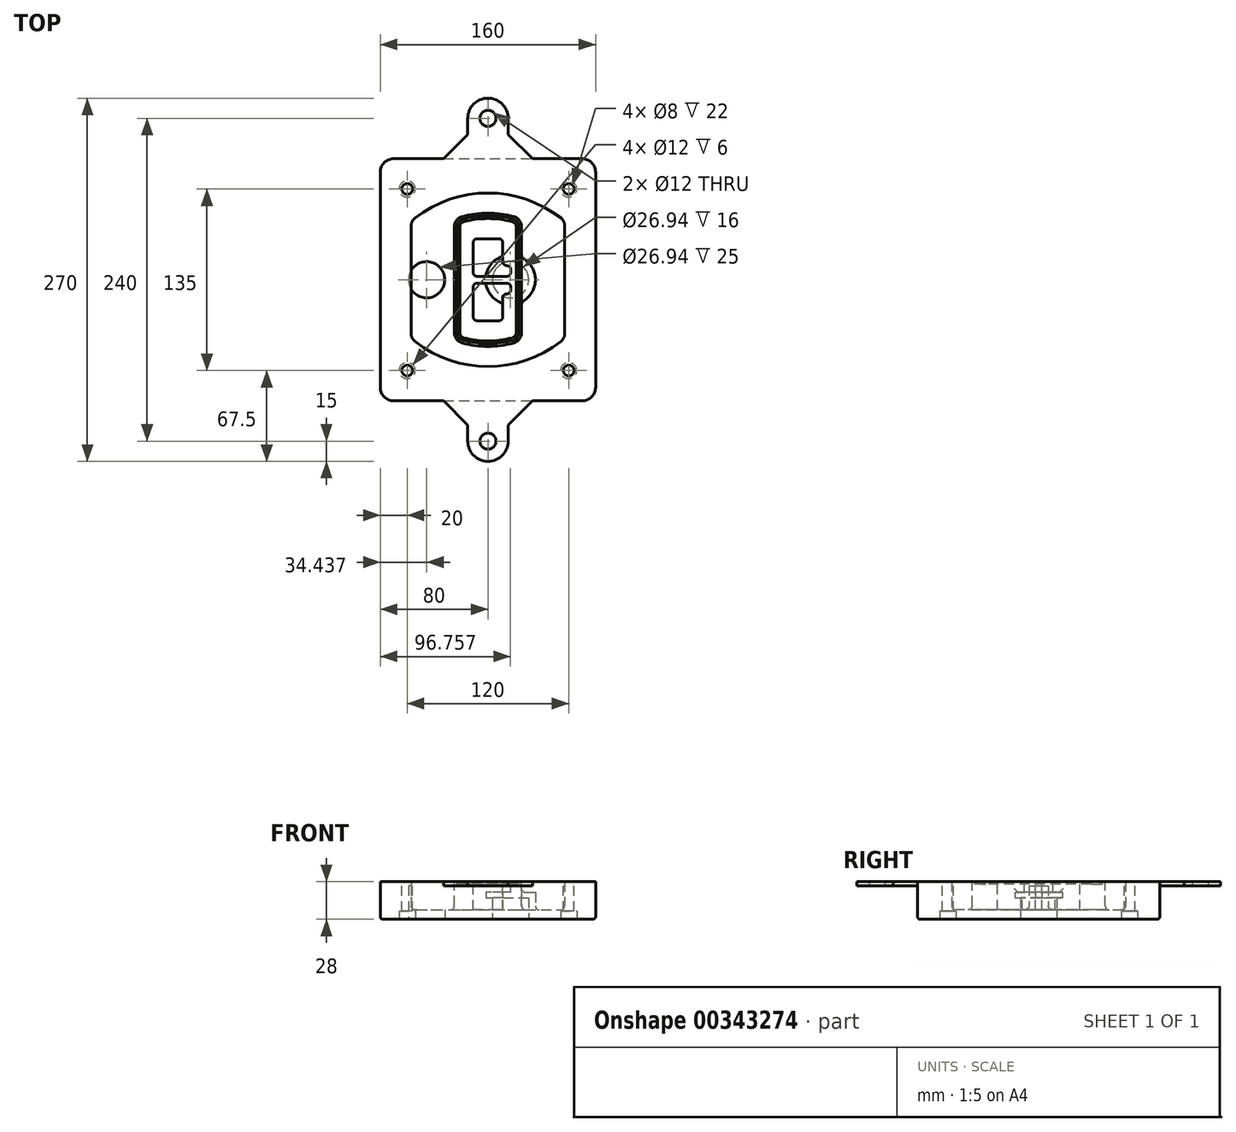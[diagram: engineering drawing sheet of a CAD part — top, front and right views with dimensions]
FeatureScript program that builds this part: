
annotation { "Feature Type Name" : "Feature", "Feature Type Description" : "" }
export const myFeature = defineFeature(function(context is Context, id is Id, definition is map)
    precondition{}
    {
        {
            var Q0;
            Q0=qCreatedBy(makeId("Top.planeOp"),FACE);
            var sketch = newSketch(context, id + "F0", { "sketchPlane" : qUnion([Q0])});
            skPoint(sketch, "E0.rect.middle", {"position": v(0, 0) * mm});
            skLineSegment(sketch, "E1.bottom", {"start": v(-70, -90) * mm, "end": v(70, -90) * mm});
            skLineSegment(sketch, "E1.top", {"start": v(-70, 90) * mm, "end": v(70, 90) * mm});
            skLineSegment(sketch, "E1.left", {"start": v(-80, -80) * mm, "end": v(-80, 80) * mm});
            skLineSegment(sketch, "E1.right", {"start": v(80, -80) * mm, "end": v(80, 80) * mm});
            skLineSegment(sketch, "E2", {"start": v(-80, 90) * mm, "end": v(80, -90) * mm, "construction": true});
            skLineSegment(sketch, "E3", {"start": v(80, 90) * mm, "end": v(-80, -90) * mm, "construction": true});
            skCircle(sketch, "E4", {"center": v(-60, 67.5) * mm, "radius": 4 * mm});
            skCircle(sketch, "E5", {"center": v(60, 67.5) * mm, "radius": 4 * mm});
            skCircle(sketch, "E6", {"center": v(60, -67.5) * mm, "radius": 4 * mm});
            skCircle(sketch, "E7", {"center": v(-60, -67.5) * mm, "radius": 4 * mm});
            skLineSegment(sketch, "E8", {"start": v(-60, 67.5) * mm, "end": v(60, 67.5) * mm, "construction": true});
            skLineSegment(sketch, "E9", {"start": v(60, 67.5) * mm, "end": v(60, -67.5) * mm, "construction": true});
            skLineSegment(sketch, "E10", {"start": v(60, -67.5) * mm, "end": v(-60, -67.5) * mm, "construction": true});
            skLineSegment(sketch, "E11", {"start": v(-60, -67.5) * mm, "end": v(-60, 67.5) * mm, "construction": true});
            skLineSegment(sketch, "E12", {"start": v(-60, 40.3) * mm, "end": v(-60, -40.3) * mm});
            skLineSegment(sketch, "E13", {"start": v(60, 40.3) * mm, "end": v(60, -40.3) * mm});
            skArc(sketch, "E14", {"start": v(56.15, 48.18) * mm, "mid": v(0, 67.5) * mm, "end": v(-56.15, 48.18) * mm});
            skArc(sketch, "E15", {"start": v(-56.15, -48.18) * mm, "mid": v(0, -67.5) * mm, "end": v(56.15, -48.18) * mm});
            skLineSegment(sketch, "E16", {"start": v(-60, 0) * mm, "end": v(60, 0) * mm, "construction": true});
            skPoint(sketch, "E17.visualSharp", {"position": v(-60, -45) * mm});
            skArc(sketch, "E17.filletArc", {"start": v(-60, -40.3) * mm, "mid": v(-58.99, -44.68) * mm, "end": v(-56.15, -48.18) * mm});
            skPoint(sketch, "E18.visualSharp", {"position": v(-60, 45) * mm});
            skArc(sketch, "E18.filletArc", {"start": v(-56.15, 48.18) * mm, "mid": v(-58.99, 44.68) * mm, "end": v(-60, 40.3) * mm});
            skPoint(sketch, "E19.visualSharp", {"position": v(60, 45) * mm});
            skArc(sketch, "E19.filletArc", {"start": v(60, 40.3) * mm, "mid": v(58.99, 44.68) * mm, "end": v(56.15, 48.18) * mm});
            skPoint(sketch, "E20.visualSharp", {"position": v(60, -45) * mm});
            skArc(sketch, "E20.filletArc", {"start": v(56.15, -48.18) * mm, "mid": v(58.99, -44.68) * mm, "end": v(60, -40.3) * mm});
            skPoint(sketch, "E21.visualSharp", {"position": v(-80, 90) * mm});
            skArc(sketch, "E21.filletArc", {"start": v(-70, 90) * mm, "mid": v(-77.07, 87.07) * mm, "end": v(-80, 80) * mm});
            skPoint(sketch, "E22.visualSharp", {"position": v(80, 90) * mm});
            skArc(sketch, "E22.filletArc", {"start": v(80, 80) * mm, "mid": v(77.07, 87.07) * mm, "end": v(70, 90) * mm});
            skPoint(sketch, "E23.visualSharp", {"position": v(80, -90) * mm});
            skArc(sketch, "E23.filletArc", {"start": v(70, -90) * mm, "mid": v(77.07, -87.07) * mm, "end": v(80, -80) * mm});
            skPoint(sketch, "E24.visualSharp", {"position": v(-80, -90) * mm});
            skArc(sketch, "E24.filletArc", {"start": v(-80, -80) * mm, "mid": v(-77.07, -87.07) * mm, "end": v(-70, -90) * mm});
            skArc(sketch, "E25.0", {"start": v(57, 40.3) * mm, "mid": v(56.3, 43.36) * mm, "end": v(54.3, 45.81) * mm});
            skLineSegment(sketch, "E25.1", {"start": v(57, 40.3) * mm, "end": v(57, -40.3) * mm});
            skArc(sketch, "E25.2", {"start": v(54.3, -45.81) * mm, "mid": v(56.3, -43.36) * mm, "end": v(57, -40.3) * mm});
            skArc(sketch, "E25.3", {"start": v(-54.3, -45.81) * mm, "mid": v(0, -64.5) * mm, "end": v(54.3, -45.81) * mm});
            skArc(sketch, "E25.4", {"start": v(-57, -40.3) * mm, "mid": v(-56.3, -43.36) * mm, "end": v(-54.3, -45.81) * mm});
            skArc(sketch, "E25.5", {"start": v(54.3, 45.81) * mm, "mid": v(0, 64.5) * mm, "end": v(-54.3, 45.81) * mm});
            skLineSegment(sketch, "E25.6", {"start": v(-57, 40.3) * mm, "end": v(-57, -40.3) * mm});
            skArc(sketch, "E25.7", {"start": v(-54.3, 45.81) * mm, "mid": v(-56.3, 43.36) * mm, "end": v(-57, 40.3) * mm});
            skArc(sketch, "E26.0", {"start": v(-58.62, 51.33) * mm, "mid": v(-62.58, 46.43) * mm, "end": v(-64, 40.3) * mm});
            skArc(sketch, "E26.1", {"start": v(58.62, 51.33) * mm, "mid": v(0, 71.5) * mm, "end": v(-58.62, 51.33) * mm});
            skArc(sketch, "E26.2", {"start": v(64, 40.3) * mm, "mid": v(62.58, 46.43) * mm, "end": v(58.62, 51.33) * mm});
            skLineSegment(sketch, "E26.3", {"start": v(64, 40.3) * mm, "end": v(64, -40.3) * mm});
            skArc(sketch, "E26.4", {"start": v(58.62, -51.33) * mm, "mid": v(62.58, -46.43) * mm, "end": v(64, -40.3) * mm});
            skLineSegment(sketch, "E26.5", {"start": v(-64, 40.3) * mm, "end": v(-64, -40.3) * mm});
            skArc(sketch, "E26.6", {"start": v(-58.62, -51.33) * mm, "mid": v(0, -71.5) * mm, "end": v(58.62, -51.33) * mm});
            skArc(sketch, "E26.7", {"start": v(-64, -40.3) * mm, "mid": v(-62.58, -46.43) * mm, "end": v(-58.62, -51.33) * mm});
            skSolve(sketch);
        }
        {
            var Q0;
            Q0=makeQuery(id+"F0.imprint","IMPRINT",FACE,{"disambiguationData":[TD([[makeQuery(id+"F0.imprint","IMPRINT",EDGE,{"derivedFrom":sQuery(id+"F0.wireOp",EDGE,"E1.bottom")}),1.0]])]});
            var Q1;
            Q1=makeQuery(id+"F0.imprint","IMPRINT",FACE,{"disambiguationData":[TD([[makeQuery(id+"F0.imprint","IMPRINT",EDGE,{"derivedFrom":sQuery(id+"F0.wireOp",EDGE,"E12")}),1.0]])]});
            var Q2;
            Q2=makeQuery(id+"F0.imprint","IMPRINT",FACE,{"disambiguationData":[TD([[makeQuery(id+"F0.imprint","IMPRINT",EDGE,{"derivedFrom":sQuery(id+"F0.wireOp",EDGE,"E25.0")}),1.0]])]});
            var Q3;
            Q3=makeQuery(id+"F0.imprint","IMPRINT",FACE,{"disambiguationData":[TD([[makeQuery(id+"F0.imprint","IMPRINT",EDGE,{"derivedFrom":sQuery(id+"F0.wireOp",EDGE,"E12")}),-1.0]])]});
            extrude(context, id + "F1", {"entities" : qUnion([Q0, Q1, Q2, Q3]), "oppositeDirection" : true, "depth" : 25 * mm});
        }
        {
            var Q0;
            Q0=makeQuery(id+"F0.imprint","IMPRINT",FACE,{"disambiguationData":[TD([[makeQuery(id+"F0.imprint","IMPRINT",EDGE,{"derivedFrom":sQuery(id+"F0.wireOp",EDGE,"E12")}),1.0]])]});
            extrude(context, id + "F2", {"entities" : qUnion([Q0]), "operationType" : NewBodyOperationType.ADD, "depth" : 3 * mm});
        }
        {
            var Q0;
            Q0=makeQuery(id+"F0.imprint","IMPRINT",FACE,{"disambiguationData":[TD([[makeQuery(id+"F0.imprint","IMPRINT",EDGE,{"derivedFrom":sQuery(id+"F0.wireOp",EDGE,"E25.0")}),1.0]])]});
            extrude(context, id + "F3", {"entities" : qUnion([Q0]), "operationType" : NewBodyOperationType.REMOVE, "oppositeDirection" : true, "depth" : 18 * mm});
        }
        {
            var Q0;
            Q0=makeQuery(id+"F2.opExtrude","CAP_FACE",FACE,{"disambiguationData":[OSD([sQuery(id+"F0.wireOp",EDGE,"E12"),sQuery(id+"F0.wireOp",EDGE,"E13"),sQuery(id+"F0.wireOp",EDGE,"E14"),sQuery(id+"F0.wireOp",EDGE,"E15"),sQuery(id+"F0.wireOp",EDGE,"E17.filletArc"),sQuery(id+"F0.wireOp",EDGE,"E18.filletArc"),sQuery(id+"F0.wireOp",EDGE,"E19.filletArc"),sQuery(id+"F0.wireOp",EDGE,"E20.filletArc"),sQuery(id+"F0.wireOp",EDGE,"E25.0"),sQuery(id+"F0.wireOp",EDGE,"E25.1"),sQuery(id+"F0.wireOp",EDGE,"E25.2"),sQuery(id+"F0.wireOp",EDGE,"E25.3"),sQuery(id+"F0.wireOp",EDGE,"E25.4"),sQuery(id+"F0.wireOp",EDGE,"E25.5"),sQuery(id+"F0.wireOp",EDGE,"E25.6"),sQuery(id+"F0.wireOp",EDGE,"E25.7")])],"isStart":false});
            var sketch = newSketch(context, id + "F4", { "sketchPlane" : qUnion([Q0])});
            skArc(sketch, "E27.0", {"start": v(-19.08, -46.97) * mm, "mid": v(0, -49.5) * mm, "end": v(19.08, -46.97) * mm});
            skArc(sketch, "E28.0", {"start": v(19.08, 46.97) * mm, "mid": v(0, 49.5) * mm, "end": v(-19.08, 46.97) * mm});
            skLineSegment(sketch, "E29", {"start": v(-25, 39.25) * mm, "end": v(-25, -39.25) * mm});
            skLineSegment(sketch, "E30", {"start": v(25, 39.25) * mm, "end": v(25, -39.25) * mm});
            skLineSegment(sketch, "E31", {"start": v(-25, 45.1) * mm, "end": v(25, 45.1) * mm, "construction": true});
            skLineSegment(sketch, "E32", {"start": v(-25, -45.1) * mm, "end": v(25, -45.1) * mm, "construction": true});
            skPoint(sketch, "E33.visualSharp", {"position": v(-25, 45.1) * mm});
            skArc(sketch, "E33.filletArc", {"start": v(-19.08, 46.97) * mm, "mid": v(-23.35, 44.11) * mm, "end": v(-25, 39.25) * mm});
            skPoint(sketch, "E34.visualSharp", {"position": v(25, 45.1) * mm});
            skArc(sketch, "E34.filletArc", {"start": v(25, 39.25) * mm, "mid": v(23.35, 44.11) * mm, "end": v(19.08, 46.97) * mm});
            skPoint(sketch, "E35.visualSharp", {"position": v(25, -45.1) * mm});
            skArc(sketch, "E35.filletArc", {"start": v(19.08, -46.97) * mm, "mid": v(23.35, -44.11) * mm, "end": v(25, -39.25) * mm});
            skPoint(sketch, "E36.visualSharp", {"position": v(-25, -45.1) * mm});
            skArc(sketch, "E36.filletArc", {"start": v(-25, -39.25) * mm, "mid": v(-23.35, -44.11) * mm, "end": v(-19.08, -46.97) * mm});
            skArc(sketch, "E37.0", {"start": v(54.3, 45.81) * mm, "mid": v(0, 64.5) * mm, "end": v(-54.3, 45.81) * mm});
            skArc(sketch, "E37.1", {"start": v(-54.3, 45.81) * mm, "mid": v(-56.3, 43.36) * mm, "end": v(-57, 40.3) * mm});
            skLineSegment(sketch, "E37.2", {"start": v(-57, 40.3) * mm, "end": v(-57, -40.3) * mm});
            skArc(sketch, "E37.3", {"start": v(-57, -40.3) * mm, "mid": v(-56.3, -43.36) * mm, "end": v(-54.3, -45.81) * mm});
            skArc(sketch, "E37.4", {"start": v(-54.3, -45.81) * mm, "mid": v(0, -64.5) * mm, "end": v(54.3, -45.81) * mm});
            skArc(sketch, "E37.5", {"start": v(54.3, -45.81) * mm, "mid": v(56.3, -43.36) * mm, "end": v(57, -40.3) * mm});
            skLineSegment(sketch, "E37.6", {"start": v(57, 40.3) * mm, "end": v(57, -40.3) * mm});
            skArc(sketch, "E37.7", {"start": v(57, 40.3) * mm, "mid": v(56.3, 43.36) * mm, "end": v(54.3, 45.81) * mm});
            skLineSegment(sketch, "E38.0", {"start": v(23, 39.25) * mm, "end": v(23, -39.25) * mm});
            skArc(sketch, "E38.1", {"start": v(18.56, -45.04) * mm, "mid": v(21.76, -42.9) * mm, "end": v(23, -39.25) * mm});
            skArc(sketch, "E38.2", {"start": v(-18.56, -45.04) * mm, "mid": v(0, -47.5) * mm, "end": v(18.56, -45.04) * mm});
            skArc(sketch, "E38.3", {"start": v(-23, -39.25) * mm, "mid": v(-21.76, -42.9) * mm, "end": v(-18.56, -45.04) * mm});
            skLineSegment(sketch, "E38.4", {"start": v(-23, 39.25) * mm, "end": v(-23, -39.25) * mm});
            skArc(sketch, "E38.5", {"start": v(23, 39.25) * mm, "mid": v(21.76, 42.9) * mm, "end": v(18.56, 45.04) * mm});
            skArc(sketch, "E38.6", {"start": v(-18.56, 45.04) * mm, "mid": v(-21.76, 42.9) * mm, "end": v(-23, 39.25) * mm});
            skArc(sketch, "E38.7", {"start": v(18.56, 45.04) * mm, "mid": v(0, 47.5) * mm, "end": v(-18.56, 45.04) * mm});
            skArc(sketch, "E39.0", {"start": v(21, 39.25) * mm, "mid": v(20.18, 41.68) * mm, "end": v(18.04, 43.1) * mm});
            skLineSegment(sketch, "E39.1", {"start": v(21, 39.25) * mm, "end": v(21, -39.25) * mm});
            skArc(sketch, "E39.2", {"start": v(18.04, -43.1) * mm, "mid": v(20.18, -41.68) * mm, "end": v(21, -39.25) * mm});
            skArc(sketch, "E39.3", {"start": v(-18.04, -43.1) * mm, "mid": v(0, -45.5) * mm, "end": v(18.04, -43.1) * mm});
            skArc(sketch, "E39.4", {"start": v(-21, -39.25) * mm, "mid": v(-20.18, -41.68) * mm, "end": v(-18.04, -43.1) * mm});
            skArc(sketch, "E39.5", {"start": v(18.04, 43.1) * mm, "mid": v(0, 45.5) * mm, "end": v(-18.04, 43.1) * mm});
            skLineSegment(sketch, "E39.6", {"start": v(-21, 39.25) * mm, "end": v(-21, -39.25) * mm});
            skArc(sketch, "E39.7", {"start": v(-18.04, 43.1) * mm, "mid": v(-20.18, 41.68) * mm, "end": v(-21, 39.25) * mm});
            skLineSegment(sketch, "E40", {"start": v(-25, 0) * mm, "end": v(25, 0) * mm, "construction": true});
            skLineSegment(sketch, "E41", {"start": v(-11, 5.5) * mm, "end": v(-11, 27.5) * mm});
            skLineSegment(sketch, "E42", {"start": v(-8, 30.5) * mm, "end": v(8, 30.5) * mm});
            skLineSegment(sketch, "E43", {"start": v(11, 27.5) * mm, "end": v(11, 13.5) * mm});
            skLineSegment(sketch, "E44", {"start": v(14, 10.5) * mm, "end": v(14, 10.5) * mm});
            skLineSegment(sketch, "E45", {"start": v(17, 7.5) * mm, "end": v(17, 5.5) * mm});
            skLineSegment(sketch, "E46", {"start": v(14, 2.5) * mm, "end": v(-8, 2.5) * mm});
            skPoint(sketch, "E47.visualSharp", {"position": v(-11, 30.5) * mm});
            skArc(sketch, "E47.filletArc", {"start": v(-8, 30.5) * mm, "mid": v(-10.12, 29.62) * mm, "end": v(-11, 27.5) * mm});
            skPoint(sketch, "E48.visualSharp", {"position": v(11, 30.5) * mm});
            skArc(sketch, "E48.filletArc", {"start": v(11, 27.5) * mm, "mid": v(10.12, 29.62) * mm, "end": v(8, 30.5) * mm});
            skPoint(sketch, "E49.visualSharp", {"position": v(11, 10.5) * mm});
            skArc(sketch, "E49.filletArc", {"start": v(11, 13.5) * mm, "mid": v(11.88, 11.38) * mm, "end": v(14, 10.5) * mm});
            skPoint(sketch, "E50.visualSharp", {"position": v(17, 10.5) * mm});
            skArc(sketch, "E50.filletArc", {"start": v(17, 7.5) * mm, "mid": v(16.12, 9.62) * mm, "end": v(14, 10.5) * mm});
            skPoint(sketch, "E51.visualSharp", {"position": v(17, 2.5) * mm});
            skArc(sketch, "E51.filletArc", {"start": v(14, 2.5) * mm, "mid": v(16.12, 3.38) * mm, "end": v(17, 5.5) * mm});
            skPoint(sketch, "E52.visualSharp", {"position": v(-11, 2.5) * mm});
            skArc(sketch, "E52.filletArc", {"start": v(-11, 5.5) * mm, "mid": v(-10.12, 3.38) * mm, "end": v(-8, 2.5) * mm});
            skLineSegment(sketch, "E53.0.MirrorCS", {"start": v(14, -2.5) * mm, "end": v(-8, -2.5) * mm});
            skArc(sketch, "E54.0.MirrorCS", {"start": v(-11, -5.5) * mm, "mid": v(-10.12, -3.38) * mm, "end": v(-8, -2.5) * mm});
            skLineSegment(sketch, "E55.0.MirrorCS", {"start": v(-11, -5.5) * mm, "end": v(-11, -27.5) * mm});
            skArc(sketch, "E56.0.MirrorCS", {"start": v(-8, -30.5) * mm, "mid": v(-10.12, -29.62) * mm, "end": v(-11, -27.5) * mm});
            skLineSegment(sketch, "E57.0.MirrorCS", {"start": v(-8, -30.5) * mm, "end": v(8, -30.5) * mm});
            skArc(sketch, "E58.0.MirrorCS", {"start": v(11, -27.5) * mm, "mid": v(10.12, -29.62) * mm, "end": v(8, -30.5) * mm});
            skLineSegment(sketch, "E59.0.MirrorCS", {"start": v(11, -27.5) * mm, "end": v(11, -13.5) * mm});
            skArc(sketch, "E60.0.MirrorCS", {"start": v(11, -13.5) * mm, "mid": v(11.88, -11.38) * mm, "end": v(14, -10.5) * mm});
            skArc(sketch, "E61.0.MirrorCS", {"start": v(17, -7.5) * mm, "mid": v(16.12, -9.62) * mm, "end": v(14, -10.5) * mm});
            skLineSegment(sketch, "E62.0.MirrorCS", {"start": v(17, -7.5) * mm, "end": v(17, -5.5) * mm});
            skArc(sketch, "E63.0.MirrorCS", {"start": v(14, -2.5) * mm, "mid": v(16.12, -3.38) * mm, "end": v(17, -5.5) * mm});
            skSolve(sketch);
        }
        {
            var Q0;
            Q0=makeQuery(id+"F4.imprint","IMPRINT",FACE,{"disambiguationData":[TD([[makeQuery(id+"F4.imprint","IMPRINT",EDGE,{"derivedFrom":sQuery(id+"F4.wireOp",EDGE,"E27.0")}),1.0]])]});
            var Q1;
            Q1=makeQuery(id+"F4.imprint","IMPRINT",FACE,{"disambiguationData":[TD([[makeQuery(id+"F4.imprint","IMPRINT",EDGE,{"derivedFrom":sQuery(id+"F4.wireOp",EDGE,"E38.0")}),-1.0]])]});
            var Q2;
            Q2=makeQuery(id+"F4.imprint","IMPRINT",FACE,{"disambiguationData":[TD([[makeQuery(id+"F4.imprint","IMPRINT",EDGE,{"derivedFrom":sQuery(id+"F4.wireOp",EDGE,"E39.0")}),1.0]])]});
            extrude(context, id + "F5", {"entities" : qUnion([Q0, Q1, Q2]), "operationType" : NewBodyOperationType.ADD, "endBound" : BoundingType.UP_TO_NEXT, "oppositeDirection" : true, "depth" : 25 * mm});
        }
        {
            var Q0;
            Q0=makeQuery(id+"F4.imprint","IMPRINT",FACE,{"disambiguationData":[TD([[makeQuery(id+"F4.imprint","IMPRINT",EDGE,{"derivedFrom":sQuery(id+"F4.wireOp",EDGE,"E38.0")}),-1.0]])]});
            extrude(context, id + "F6", {"entities" : qUnion([Q0]), "operationType" : NewBodyOperationType.REMOVE, "oppositeDirection" : true, "depth" : 2 * mm});
        }
        {
            var Q0;
            Q0=makeQuery(id+"F1.opExtrude","CAP_FACE",FACE,{"disambiguationData":[OSD([sQuery(id+"F0.wireOp",EDGE,"E1.bottom"),sQuery(id+"F0.wireOp",EDGE,"E1.top"),sQuery(id+"F0.wireOp",EDGE,"E1.left"),sQuery(id+"F0.wireOp",EDGE,"E1.right"),sQuery(id+"F0.wireOp",EDGE,"E4"),sQuery(id+"F0.wireOp",EDGE,"E5"),sQuery(id+"F0.wireOp",EDGE,"E6"),sQuery(id+"F0.wireOp",EDGE,"E7"),sQuery(id+"F0.wireOp",EDGE,"E21.filletArc"),sQuery(id+"F0.wireOp",EDGE,"E22.filletArc"),sQuery(id+"F0.wireOp",EDGE,"E23.filletArc"),sQuery(id+"F0.wireOp",EDGE,"E24.filletArc")])],"isStart":false});
            var sketch = newSketch(context, id + "F7", { "sketchPlane" : qUnion([Q0])});
            skCircle(sketch, "E64", {"center": v(16.76, 0) * mm, "radius": 13.47 * mm});
            skCircle(sketch, "E65", {"center": v(-45.56, 0) * mm, "radius": 13.47 * mm});
            skLineSegment(sketch, "E66", {"start": v(80, 0) * mm, "end": v(-80, 0) * mm});
            skCircle(sketch, "E67", {"center": v(16.76, 0) * mm, "radius": 18.47 * mm});
            skCircle(sketch, "E68", {"center": v(60, -67.5) * mm, "radius": 6 * mm});
            skCircle(sketch, "E69", {"center": v(-60, -67.5) * mm, "radius": 6 * mm});
            skCircle(sketch, "E70", {"center": v(-60, 67.5) * mm, "radius": 6 * mm});
            skCircle(sketch, "E71", {"center": v(60, 67.5) * mm, "radius": 6 * mm});
            skSolve(sketch);
        }
        {
            var Q0;
            {var subQ1=sQuery(id+"F7.wireOp",EDGE,"E66");var subQ4=sQuery(id+"F7.wireOp",EDGE,"E64");var subQ6=makeQuery(id+"F7.imprint","INTERSECT",VERTEX,{"disambiguationData":[OD(0.0)],"derivedFrom":[subQ4,subQ1]});Q0=makeQuery(id+"F7.imprint","IMPRINT",FACE,{"disambiguationData":[TD([[makeQuery(id+"F7.imprint","IMPRINT",EDGE,{"disambiguationData":[TD([[subQ6,-1.0]])],"derivedFrom":subQ4}),-1.0]])]});}
            var Q1;
            {var subQ0=sQuery(id+"F7.wireOp",EDGE,"E66");var subQ1=sQuery(id+"F7.wireOp",EDGE,"E64");var subQ3=makeQuery(id+"F7.imprint","INTERSECT",VERTEX,{"disambiguationData":[OD(0.0)],"derivedFrom":[subQ1,subQ0]});Q1=makeQuery(id+"F7.imprint","IMPRINT",FACE,{"disambiguationData":[TD([[makeQuery(id+"F7.imprint","IMPRINT",EDGE,{"disambiguationData":[TD([[subQ3,-1.0]])],"derivedFrom":subQ1}),1.0]])]});}
            var Q2;
            {var subQ0=sQuery(id+"F7.wireOp",EDGE,"E66");var subQ1=sQuery(id+"F7.wireOp",EDGE,"E64");var subQ3=makeQuery(id+"F7.imprint","INTERSECT",VERTEX,{"disambiguationData":[OD(0.0)],"derivedFrom":[subQ1,subQ0]});Q2=makeQuery(id+"F7.imprint","IMPRINT",FACE,{"disambiguationData":[TD([[makeQuery(id+"F7.imprint","IMPRINT",EDGE,{"disambiguationData":[TD([[subQ3,1.0]])],"derivedFrom":subQ1}),1.0]])]});}
            var Q3;
            {var subQ1=sQuery(id+"F7.wireOp",EDGE,"E66");var subQ4=sQuery(id+"F7.wireOp",EDGE,"E64");var subQ6=makeQuery(id+"F7.imprint","INTERSECT",VERTEX,{"disambiguationData":[OD(0.0)],"derivedFrom":[subQ4,subQ1]});Q3=makeQuery(id+"F7.imprint","IMPRINT",FACE,{"disambiguationData":[TD([[makeQuery(id+"F7.imprint","IMPRINT",EDGE,{"disambiguationData":[TD([[subQ6,1.0]])],"derivedFrom":subQ4}),-1.0]])]});}
            extrude(context, id + "F8", {"entities" : qUnion([Q0, Q1, Q2, Q3]), "operationType" : NewBodyOperationType.ADD, "oppositeDirection" : true, "depth" : 20 * mm});
        }
        {
            var Q0;
            {var subQ0=sQuery(id+"F7.wireOp",EDGE,"E66");var subQ1=sQuery(id+"F7.wireOp",EDGE,"E64");var subQ3=makeQuery(id+"F7.imprint","INTERSECT",VERTEX,{"disambiguationData":[OD(0.0)],"derivedFrom":[subQ1,subQ0]});Q0=makeQuery(id+"F7.imprint","IMPRINT",FACE,{"disambiguationData":[TD([[makeQuery(id+"F7.imprint","IMPRINT",EDGE,{"disambiguationData":[TD([[subQ3,-1.0]])],"derivedFrom":subQ1}),1.0]])]});}
            var Q1;
            {var subQ0=sQuery(id+"F7.wireOp",EDGE,"E66");var subQ1=sQuery(id+"F7.wireOp",EDGE,"E64");var subQ3=makeQuery(id+"F7.imprint","INTERSECT",VERTEX,{"disambiguationData":[OD(0.0)],"derivedFrom":[subQ1,subQ0]});Q1=makeQuery(id+"F7.imprint","IMPRINT",FACE,{"disambiguationData":[TD([[makeQuery(id+"F7.imprint","IMPRINT",EDGE,{"disambiguationData":[TD([[subQ3,1.0]])],"derivedFrom":subQ1}),1.0]])]});}
            extrude(context, id + "F9", {"entities" : qUnion([Q0, Q1]), "operationType" : NewBodyOperationType.REMOVE, "oppositeDirection" : true, "depth" : 16 * mm});
        }
        {
            var Q0;
            {var subQ0=sQuery(id+"F7.wireOp",EDGE,"E66");var subQ1=sQuery(id+"F7.wireOp",EDGE,"E65");var subQ3=makeQuery(id+"F7.imprint","INTERSECT",VERTEX,{"disambiguationData":[OD(0.0)],"derivedFrom":[subQ1,subQ0]});Q0=makeQuery(id+"F7.imprint","IMPRINT",FACE,{"disambiguationData":[TD([[makeQuery(id+"F7.imprint","IMPRINT",EDGE,{"disambiguationData":[TD([[subQ3,-1.0]])],"derivedFrom":subQ1}),1.0]])]});}
            var Q1;
            {var subQ0=sQuery(id+"F7.wireOp",EDGE,"E66");var subQ1=sQuery(id+"F7.wireOp",EDGE,"E65");var subQ3=makeQuery(id+"F7.imprint","INTERSECT",VERTEX,{"disambiguationData":[OD(0.0)],"derivedFrom":[subQ1,subQ0]});Q1=makeQuery(id+"F7.imprint","IMPRINT",FACE,{"disambiguationData":[TD([[makeQuery(id+"F7.imprint","IMPRINT",EDGE,{"disambiguationData":[TD([[subQ3,1.0]])],"derivedFrom":subQ1}),1.0]])]});}
            extrude(context, id + "F10", {"entities" : qUnion([Q0, Q1]), "operationType" : NewBodyOperationType.REMOVE, "oppositeDirection" : true, "depth" : 25 * mm});
        }
        {
            var Q0;
            Q0=makeQuery(id+"F7.imprint","IMPRINT",FACE,{"disambiguationData":[TD([[makeQuery(id+"F7.imprint","IMPRINT",EDGE,{"derivedFrom":sQuery(id+"F7.wireOp",EDGE,"E68")}),1.0]])]});
            var Q1;
            Q1=makeQuery(id+"F7.imprint","IMPRINT",FACE,{"disambiguationData":[TD([[makeQuery(id+"F7.imprint","IMPRINT",EDGE,{"derivedFrom":makeQuery(id+"F1.opExtrude","CAP_EDGE",EDGE,{"disambiguationData":[OSD([sQuery(id+"F0.wireOp",EDGE,"E5")])],"isStart":false})}),-1.0]])]});
            var Q2;
            Q2=makeQuery(id+"F7.imprint","IMPRINT",FACE,{"disambiguationData":[TD([[makeQuery(id+"F7.imprint","IMPRINT",EDGE,{"derivedFrom":sQuery(id+"F7.wireOp",EDGE,"E69")}),1.0]])]});
            var Q3;
            Q3=makeQuery(id+"F7.imprint","IMPRINT",FACE,{"disambiguationData":[TD([[makeQuery(id+"F7.imprint","IMPRINT",EDGE,{"derivedFrom":makeQuery(id+"F1.opExtrude","CAP_EDGE",EDGE,{"disambiguationData":[OSD([sQuery(id+"F0.wireOp",EDGE,"E4")])],"isStart":false})}),-1.0]])]});
            var Q4;
            Q4=makeQuery(id+"F7.imprint","IMPRINT",FACE,{"disambiguationData":[TD([[makeQuery(id+"F7.imprint","IMPRINT",EDGE,{"derivedFrom":sQuery(id+"F7.wireOp",EDGE,"E70")}),1.0]])]});
            var Q5;
            Q5=makeQuery(id+"F7.imprint","IMPRINT",FACE,{"disambiguationData":[TD([[makeQuery(id+"F7.imprint","IMPRINT",EDGE,{"derivedFrom":makeQuery(id+"F1.opExtrude","CAP_EDGE",EDGE,{"disambiguationData":[OSD([sQuery(id+"F0.wireOp",EDGE,"E7")])],"isStart":false})}),-1.0]])]});
            var Q6;
            Q6=makeQuery(id+"F7.imprint","IMPRINT",FACE,{"disambiguationData":[TD([[makeQuery(id+"F7.imprint","IMPRINT",EDGE,{"derivedFrom":sQuery(id+"F7.wireOp",EDGE,"E71")}),1.0]])]});
            var Q7;
            Q7=makeQuery(id+"F7.imprint","IMPRINT",FACE,{"disambiguationData":[TD([[makeQuery(id+"F7.imprint","IMPRINT",EDGE,{"derivedFrom":makeQuery(id+"F1.opExtrude","CAP_EDGE",EDGE,{"disambiguationData":[OSD([sQuery(id+"F0.wireOp",EDGE,"E6")])],"isStart":false})}),-1.0]])]});
            extrude(context, id + "F11", {"entities" : qUnion([Q0, Q1, Q2, Q3, Q4, Q5, Q6, Q7]), "operationType" : NewBodyOperationType.REMOVE, "oppositeDirection" : true, "depth" : 6 * mm});
        }
        {
            var Q0;
            Q0=makeQuery(id+"F9.boolean.opBoolean","COPY",FACE,{"derivedFrom":makeQuery(id+"F9.opExtrude","CAP_FACE",FACE,{"disambiguationData":[OSD([sQuery(id+"F7.wireOp",EDGE,"E64")])],"isStart":false})});
            var sketch = newSketch(context, id + "F12", { "sketchPlane" : qUnion([Q0])});
            skArc(sketch, "E72.0", {"start": v(11, 17.55) * mm, "mid": v(2.57, 11.82) * mm, "end": v(-1.54, 2.5) * mm});
            skArc(sketch, "E72.1", {"start": v(-1.54, -2.5) * mm, "mid": v(2.57, -11.82) * mm, "end": v(11, -17.55) * mm});
            skLineSegment(sketch, "E73", {"start": v(-1.54, -2.5) * mm, "end": v(14, -2.5) * mm});
            skLineSegment(sketch, "E74.0", {"start": v(14, 2.5) * mm, "end": v(-1.54, 2.5) * mm});
            skArc(sketch, "E74.1", {"start": v(14, 2.5) * mm, "mid": v(16.12, 3.38) * mm, "end": v(17, 5.5) * mm});
            skLineSegment(sketch, "E74.2", {"start": v(17, 7.5) * mm, "end": v(17, 5.5) * mm});
            skArc(sketch, "E74.3", {"start": v(17, 7.5) * mm, "mid": v(16.12, 9.62) * mm, "end": v(14, 10.5) * mm});
            skArc(sketch, "E74.4", {"start": v(11, 13.5) * mm, "mid": v(11.88, 11.38) * mm, "end": v(14, 10.5) * mm});
            skLineSegment(sketch, "E74.5", {"start": v(11, 17.55) * mm, "end": v(11, 13.5) * mm});
            skLineSegment(sketch, "E74.7", {"start": v(14, -2.5) * mm, "end": v(-1.54, -2.5) * mm});
            skArc(sketch, "E74.8", {"start": v(14, -2.5) * mm, "mid": v(16.12, -3.38) * mm, "end": v(17, -5.5) * mm});
            skLineSegment(sketch, "E74.9", {"start": v(17, -7.5) * mm, "end": v(17, -5.5) * mm});
            skArc(sketch, "E74.10", {"start": v(17, -7.5) * mm, "mid": v(16.12, -9.62) * mm, "end": v(14, -10.5) * mm});
            skArc(sketch, "E74.11", {"start": v(11, -13.5) * mm, "mid": v(11.88, -11.38) * mm, "end": v(14, -10.5) * mm});
            skLineSegment(sketch, "E74.12", {"start": v(11, -17.55) * mm, "end": v(11, -13.5) * mm});
            skPoint(sketch, "E75.orphan", {"position": v(11, -27.5) * mm});
            skPoint(sketch, "E76.orphan", {"position": v(-8, -2.5) * mm});
            skPoint(sketch, "E77.orphan", {"position": v(-8, 2.5) * mm});
            skPoint(sketch, "E78.orphan", {"position": v(11, 27.5) * mm});
            skSolve(sketch);
        }
        {
            var Q0;
            {var subQ7=sQuery(id+"F12.wireOp",EDGE,"E72.0");var subQ14=sQuery(id+"F12.wireOp",EDGE,"E72.1");var subQ16=sQuery(id+"F12.wireOp",EDGE,"E74.1");var subQ18=sQuery(id+"F12.wireOp",EDGE,"E74.8");Q0=qUnion([makeQuery(id+"F12.imprint","IMPRINT",FACE,{"disambiguationData":[TD([[makeQuery(id+"F12.imprint","IMPRINT",EDGE,{"derivedFrom":subQ7}),1.0]])]}),makeQuery(id+"F12.imprint","IMPRINT",FACE,{"disambiguationData":[TD([[makeQuery(id+"F12.imprint","IMPRINT",EDGE,{"derivedFrom":subQ14}),1.0]])]}),makeQuery(id+"F12.imprint","IMPRINT",FACE,{"disambiguationData":[TD([[makeQuery(id+"F12.imprint","IMPRINT",EDGE,{"derivedFrom":subQ16}),1.0]])]}),makeQuery(id+"F12.imprint","IMPRINT",FACE,{"disambiguationData":[TD([[makeQuery(id+"F12.imprint","IMPRINT",EDGE,{"derivedFrom":subQ18}),-1.0]])]})]);}
            var Q1;
            Q1=makeQuery(id+"F5.boolean.opBoolean","SPLIT",FACE,{"disambiguationData":[TD([makeQuery(id+"F5.opExtrude","SWEPT_FACE",FACE,{"disambiguationData":[OSD([sQuery(id+"F4.wireOp",EDGE,"E41")])]})])],"derivedFrom":makeQuery(id+"F3.boolean.opBoolean","COPY",FACE,{"derivedFrom":makeQuery(id+"F3.opExtrude","CAP_FACE",FACE,{"disambiguationData":[OSD([sQuery(id+"F0.wireOp",EDGE,"E25.0"),sQuery(id+"F0.wireOp",EDGE,"E25.1"),sQuery(id+"F0.wireOp",EDGE,"E25.2"),sQuery(id+"F0.wireOp",EDGE,"E25.3"),sQuery(id+"F0.wireOp",EDGE,"E25.4"),sQuery(id+"F0.wireOp",EDGE,"E25.5"),sQuery(id+"F0.wireOp",EDGE,"E25.6"),sQuery(id+"F0.wireOp",EDGE,"E25.7")])],"isStart":false})})});
            extrude(context, id + "F13", {"entities" : qUnion([Q0]), "operationType" : NewBodyOperationType.REMOVE, "endBound" : BoundingType.UP_TO_SURFACE, "endBoundEntityFace" : qUnion([Q1]), "depth" : 25 * mm});
        }
        {
            var Q0;
            Q0=makeQuery(id+"F3.boolean.opBoolean","COPY",EDGE,{"derivedFrom":makeQuery(id+"F3.opExtrude","CAP_EDGE",EDGE,{"disambiguationData":[OSD([sQuery(id+"F0.wireOp",EDGE,"E25.6")])],"isStart":false})});
            var Q1;
            Q1=makeQuery(id+"F8.boolean.opBoolean","INTERSECT",EDGE,{"derivedFrom":[makeQuery(id+"F5.opExtrude","SWEPT_FACE",FACE,{"disambiguationData":[OSD([sQuery(id+"F4.wireOp",EDGE,"E30")])]}),makeQuery(id+"F8.opExtrude","CAP_FACE",FACE,{"disambiguationData":[OSD([sQuery(id+"F7.wireOp",EDGE,"E67")])],"isStart":false})]});
            var Q2;
            Q2=makeQuery(id+"F8.boolean.opBoolean","INTERSECT",EDGE,{"disambiguationData":[OD(1.0)],"derivedFrom":[makeQuery(id+"F5.opExtrude","SWEPT_FACE",FACE,{"disambiguationData":[OSD([sQuery(id+"F4.wireOp",EDGE,"E30")])]}),makeQuery(id+"F8.opExtrude","SWEPT_FACE",FACE,{"disambiguationData":[OSD([sQuery(id+"F7.wireOp",EDGE,"E67")])]})]});
            var Q3;
            {var subQ0=sQuery(id+"F4.wireOp",EDGE,"E30");Q3=makeQuery(id+"F8.boolean.opBoolean","SPLIT",EDGE,{"disambiguationData":[TD([makeQuery(id+"F5.opExtrude","SWEPT_FACE",FACE,{"disambiguationData":[OSD([sQuery(id+"F4.wireOp",EDGE,"E35.filletArc")])]})])],"derivedFrom":makeQuery(id+"F5.opExtrude","CAP_EDGE",EDGE,{"disambiguationData":[OSD([subQ0])],"isStart":false})});}
            var Q4;
            {var subQ0=sQuery(id+"F0.wireOp",EDGE,"E25.7");var subQ1=sQuery(id+"F0.wireOp",EDGE,"E25.1");var subQ2=sQuery(id+"F0.wireOp",EDGE,"E25.6");var subQ3=sQuery(id+"F0.wireOp",EDGE,"E25.5");var subQ4=sQuery(id+"F0.wireOp",EDGE,"E25.4");var subQ5=sQuery(id+"F0.wireOp",EDGE,"E25.0");var subQ6=sQuery(id+"F0.wireOp",EDGE,"E25.2");var subQ7=sQuery(id+"F0.wireOp",EDGE,"E25.3");Q4=makeQuery(id+"F8.boolean.opBoolean","INTERSECT",EDGE,{"derivedFrom":[makeQuery(id+"F5.boolean.opBoolean","SPLIT",FACE,{"disambiguationData":[TD([makeQuery(id+"F2.opExtrude","SWEPT_FACE",FACE,{"disambiguationData":[OSD([subQ5])]})])],"derivedFrom":makeQuery(id+"F3.boolean.opBoolean","COPY",FACE,{"derivedFrom":makeQuery(id+"F3.opExtrude","CAP_FACE",FACE,{"disambiguationData":[OSD([subQ5,subQ1,subQ6,subQ7,subQ4,subQ3,subQ2,subQ0])],"isStart":false})})}),makeQuery(id+"F8.opExtrude","SWEPT_FACE",FACE,{"disambiguationData":[OSD([sQuery(id+"F7.wireOp",EDGE,"E67")])]})]});}
            var Q5;
            Q5=makeQuery(id+"F8.boolean.opBoolean","INTERSECT",EDGE,{"disambiguationData":[OD(0.0)],"derivedFrom":[makeQuery(id+"F5.opExtrude","SWEPT_FACE",FACE,{"disambiguationData":[OSD([sQuery(id+"F4.wireOp",EDGE,"E30")])]}),makeQuery(id+"F8.opExtrude","SWEPT_FACE",FACE,{"disambiguationData":[OSD([sQuery(id+"F7.wireOp",EDGE,"E67")])]})]});
            fillet(context, id + "F14", {"entities" : qUnion([Q0, Q1, Q2, Q3, Q4, Q5]), "radius" : 3 * mm, "tangentPropagation" : true, "allowEdgeOverflow" : false});
        }
        {
            var Q0;
            Q0=makeQuery(id+"F1.opExtrude","CAP_EDGE",EDGE,{"disambiguationData":[OSD([sQuery(id+"F0.wireOp",EDGE,"E1.bottom")])],"isStart":false});
            fillet(context, id + "F15", {"entities" : qUnion([Q0]), "radius" : 2 * mm, "tangentPropagation" : true, "allowEdgeOverflow" : false});
        }
        {
            var Q0;
            {var subQ0=sQuery(id+"F0.wireOp",EDGE,"E21.filletArc");var subQ1=sQuery(id+"F0.wireOp",EDGE,"E7");var subQ2=sQuery(id+"F0.wireOp",EDGE,"E6");var subQ3=sQuery(id+"F0.wireOp",EDGE,"E5");var subQ4=sQuery(id+"F0.wireOp",EDGE,"E4");var subQ5=sQuery(id+"F0.wireOp",EDGE,"E22.filletArc");var subQ6=sQuery(id+"F0.wireOp",EDGE,"E1.bottom");var subQ7=sQuery(id+"F0.wireOp",EDGE,"E1.right");var subQ8=sQuery(id+"F0.wireOp",EDGE,"E1.top");var subQ9=sQuery(id+"F0.wireOp",EDGE,"E1.left");var subQ10=sQuery(id+"F0.wireOp",EDGE,"E23.filletArc");var subQ11=sQuery(id+"F0.wireOp",EDGE,"E24.filletArc");Q0=makeQuery(id+"F2.boolean.opBoolean","SPLIT",FACE,{"disambiguationData":[TD([makeQuery(id+"F1.opExtrude","SWEPT_FACE",FACE,{"disambiguationData":[OSD([subQ6])]})])],"derivedFrom":makeQuery(id+"F1.opExtrude","CAP_FACE",FACE,{"disambiguationData":[OSD([subQ6,subQ8,subQ9,subQ7,subQ4,subQ3,subQ2,subQ1,subQ0,subQ5,subQ10,subQ11])],"isStart":true})});}
            var sketch = newSketch(context, id + "F16", { "sketchPlane" : qUnion([Q0])});
            skLineSegment(sketch, "E79.0", {"start": v(-70, 90) * mm, "end": v(70, 90) * mm});
            skArc(sketch, "E79.1", {"start": v(-70, 90) * mm, "mid": v(-77.07, 87.07) * mm, "end": v(-80, 80) * mm});
            skArc(sketch, "E79.2", {"start": v(80, 80) * mm, "mid": v(77.07, 87.07) * mm, "end": v(70, 90) * mm});
            skLineSegment(sketch, "E79.3", {"start": v(80, -80) * mm, "end": v(80, 80) * mm});
            skArc(sketch, "E79.4", {"start": v(70, -90) * mm, "mid": v(77.07, -87.07) * mm, "end": v(80, -80) * mm});
            skLineSegment(sketch, "E79.5", {"start": v(-70, -90) * mm, "end": v(70, -90) * mm});
            skArc(sketch, "E79.6", {"start": v(-80, -80) * mm, "mid": v(-77.07, -87.07) * mm, "end": v(-70, -90) * mm});
            skLineSegment(sketch, "E79.7", {"start": v(-80, -80) * mm, "end": v(-80, 80) * mm});
            skCircle(sketch, "E79.8", {"center": v(-60, 67.5) * mm, "radius": 4 * mm});
            skCircle(sketch, "E79.9", {"center": v(60, 67.5) * mm, "radius": 4 * mm});
            skCircle(sketch, "E79.10", {"center": v(60, -67.5) * mm, "radius": 4 * mm});
            skCircle(sketch, "E79.11", {"center": v(-60, -67.5) * mm, "radius": 4 * mm});
            skLineSegment(sketch, "E79.12", {"start": v(-60, 40.3) * mm, "end": v(-60, -40.3) * mm});
            skArc(sketch, "E79.13", {"start": v(56.15, 48.18) * mm, "mid": v(0, 67.5) * mm, "end": v(-56.15, 48.18) * mm});
            skArc(sketch, "E79.14", {"start": v(-56.15, 48.18) * mm, "mid": v(-58.99, 44.68) * mm, "end": v(-60, 40.3) * mm});
            skArc(sketch, "E79.15", {"start": v(60, 40.3) * mm, "mid": v(58.99, 44.68) * mm, "end": v(56.15, 48.18) * mm});
            skLineSegment(sketch, "E79.16", {"start": v(60, 40.3) * mm, "end": v(60, -40.3) * mm});
            skArc(sketch, "E79.17", {"start": v(56.15, -48.18) * mm, "mid": v(58.99, -44.68) * mm, "end": v(60, -40.3) * mm});
            skArc(sketch, "E79.18", {"start": v(-56.15, -48.18) * mm, "mid": v(0, -67.5) * mm, "end": v(56.15, -48.18) * mm});
            skArc(sketch, "E79.19", {"start": v(-60, -40.3) * mm, "mid": v(-58.99, -44.68) * mm, "end": v(-56.15, -48.18) * mm});
            skLineSegment(sketch, "E80", {"start": v(-33, 90) * mm, "end": v(-15, 108) * mm});
            skLineSegment(sketch, "E81", {"start": v(33, 90) * mm, "end": v(15, 108) * mm});
            skCircle(sketch, "E82", {"center": v(0, 120) * mm, "radius": 6 * mm});
            skLineSegment(sketch, "E83", {"start": v(0, 120) * mm, "end": v(0, 90) * mm, "construction": true});
            skLineSegment(sketch, "E84", {"start": v(-15, 108) * mm, "end": v(-15, 120) * mm});
            skLineSegment(sketch, "E85", {"start": v(15, 108) * mm, "end": v(15, 120) * mm});
            skArc(sketch, "E86", {"start": v(15, 120) * mm, "mid": v(0, 135) * mm, "end": v(-15, 120) * mm});
            skLineSegment(sketch, "E87", {"start": v(80, 0) * mm, "end": v(-80, 0) * mm, "construction": true});
            skLineSegment(sketch, "E88.MirrorCS", {"start": v(-33, -90) * mm, "end": v(-15, -108) * mm});
            skLineSegment(sketch, "E89.MirrorCS", {"start": v(-15, -108) * mm, "end": v(-15, -120) * mm});
            skArc(sketch, "E90.MirrorCS", {"start": v(15, -120) * mm, "mid": v(0, -135) * mm, "end": v(-15, -120) * mm});
            skCircle(sketch, "E91.MirrorC", {"center": v(0, -120) * mm, "radius": 6 * mm});
            skLineSegment(sketch, "E92.MirrorCS", {"start": v(15, -108) * mm, "end": v(15, -120) * mm});
            skLineSegment(sketch, "E93.MirrorCS", {"start": v(33, -90) * mm, "end": v(15, -108) * mm});
            skLineSegment(sketch, "E94.MirrorCS", {"start": v(0, -120) * mm, "end": v(0, -90) * mm, "construction": true});
            skSolve(sketch);
        }
        {
            var Q0;
            Q0 = qSketchRegion(id + "F16", true);
            var Q1;
            Q1=makeQuery(id+"F2.opExtrude","CAP_FACE",FACE,{"disambiguationData":[OSD([sQuery(id+"F0.wireOp",EDGE,"E12"),sQuery(id+"F0.wireOp",EDGE,"E13"),sQuery(id+"F0.wireOp",EDGE,"E14"),sQuery(id+"F0.wireOp",EDGE,"E15"),sQuery(id+"F0.wireOp",EDGE,"E17.filletArc"),sQuery(id+"F0.wireOp",EDGE,"E18.filletArc"),sQuery(id+"F0.wireOp",EDGE,"E19.filletArc"),sQuery(id+"F0.wireOp",EDGE,"E20.filletArc"),sQuery(id+"F0.wireOp",EDGE,"E25.0"),sQuery(id+"F0.wireOp",EDGE,"E25.1"),sQuery(id+"F0.wireOp",EDGE,"E25.2"),sQuery(id+"F0.wireOp",EDGE,"E25.3"),sQuery(id+"F0.wireOp",EDGE,"E25.4"),sQuery(id+"F0.wireOp",EDGE,"E25.5"),sQuery(id+"F0.wireOp",EDGE,"E25.6"),sQuery(id+"F0.wireOp",EDGE,"E25.7")])],"isStart":false});
            extrude(context, id + "F17", {"entities" : qUnion([Q0]), "operationType" : NewBodyOperationType.ADD, "endBound" : BoundingType.UP_TO_SURFACE, "endBoundEntityFace" : qUnion([Q1]), "depth" : 25 * mm});
        }
    });
